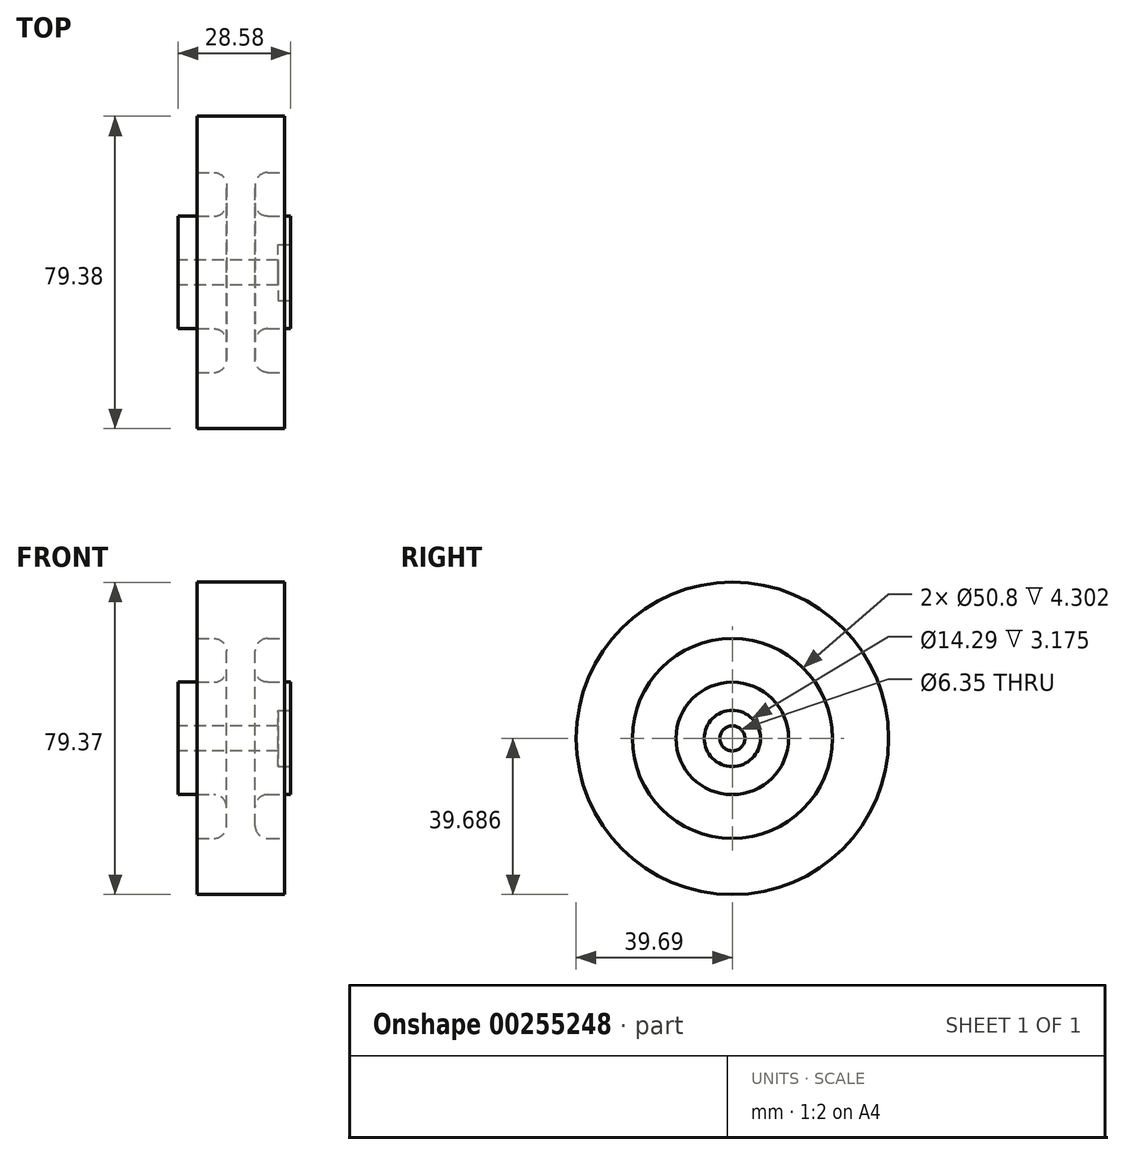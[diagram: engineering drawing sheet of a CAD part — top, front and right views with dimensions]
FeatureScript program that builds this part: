
annotation { "Feature Type Name" : "Feature", "Feature Type Description" : "" }
export const myFeature = defineFeature(function(context is Context, id is Id, definition is map)
    precondition{}
    {
        {
            var Q0;
            Q0=qCreatedBy(makeId("Front.planeOp"),FACE);
            var sketch = newSketch(context, id + "F0", { "sketchPlane" : qUnion([Q0])});
            skLineSegment(sketch, "E0", {"start": v(0, 0) * mm, "end": v(-12.7, 0) * mm});
            skLineSegment(sketch, "E1", {"start": v(-12.7, 0) * mm, "end": v(-12.7, 7.14) * mm});
            skLineSegment(sketch, "E2", {"start": v(-12.7, 7.14) * mm, "end": v(-6.81, 7.14) * mm});
            skLineSegment(sketch, "E3", {"start": v(-3.64, 10.32) * mm, "end": v(-3.64, 15.08) * mm});
            skLineSegment(sketch, "E4", {"start": v(-6.81, 18.26) * mm, "end": v(-11.11, 18.26) * mm});
            skLineSegment(sketch, "E5", {"start": v(-11.11, 18.26) * mm, "end": v(-11.11, 32.54) * mm});
            skLineSegment(sketch, "E6", {"start": v(-11.11, 32.54) * mm, "end": v(0, 32.54) * mm});
            skLineSegment(sketch, "E7", {"start": v(0, 32.54) * mm, "end": v(0, 0) * mm});
            skLineSegment(sketch, "E8", {"start": v(0, 0) * mm, "end": v(0, -7.14) * mm, "construction": true});
            skLineSegment(sketch, "E9", {"start": v(0, -7.14) * mm, "end": v(-25.49, -7.14) * mm, "construction": true});
            skPoint(sketch, "E10.visualSharp", {"position": v(-3.64, 18.26) * mm});
            skArc(sketch, "E10.filletArc", {"start": v(-3.64, 15.08) * mm, "mid": v(-4.56, 17.33) * mm, "end": v(-6.81, 18.26) * mm});
            skPoint(sketch, "E11.visualSharp", {"position": v(-3.64, 7.14) * mm});
            skArc(sketch, "E11.filletArc", {"start": v(-6.81, 7.14) * mm, "mid": v(-4.56, 8.07) * mm, "end": v(-3.64, 10.32) * mm});
            skLineSegment(sketch, "E12.MirrorCS", {"start": v(11.11, 32.54) * mm, "end": v(0, 32.54) * mm});
            skLineSegment(sketch, "E13.MirrorCS", {"start": v(11.11, 18.26) * mm, "end": v(11.11, 32.54) * mm});
            skLineSegment(sketch, "E14.MirrorCS", {"start": v(6.81, 18.26) * mm, "end": v(11.11, 18.26) * mm});
            skArc(sketch, "E15.MirrorCS", {"start": v(3.64, 15.08) * mm, "mid": v(4.56, 17.33) * mm, "end": v(6.81, 18.26) * mm});
            skLineSegment(sketch, "E16.MirrorCS", {"start": v(3.64, 10.32) * mm, "end": v(3.64, 15.08) * mm});
            skArc(sketch, "E17.MirrorCS", {"start": v(6.81, 7.14) * mm, "mid": v(4.56, 8.07) * mm, "end": v(3.64, 10.32) * mm});
            skLineSegment(sketch, "E18.MirrorCS", {"start": v(12.7, 7.14) * mm, "end": v(6.81, 7.14) * mm});
            skLineSegment(sketch, "E19.MirrorCS", {"start": v(12.7, 0) * mm, "end": v(12.7, 7.14) * mm});
            skLineSegment(sketch, "E20.MirrorCS", {"start": v(0, 0) * mm, "end": v(12.7, 0) * mm});
            skSolve(sketch);
        }
        {
            var Q0;
            Q0=makeQuery(id+"F0.imprint","IMPRINT",FACE,{"disambiguationData":[TD([[makeQuery(id+"F0.imprint","IMPRINT",EDGE,{"derivedFrom":sQuery(id+"F0.wireOp",EDGE,"E0")}),-1.0]])]});
            var Q1;
            Q1=makeQuery(id+"F0.imprint","IMPRINT",FACE,{"disambiguationData":[TD([[makeQuery(id+"F0.imprint","IMPRINT",EDGE,{"derivedFrom":sQuery(id+"F0.wireOp",EDGE,"E7")}),1.0]])]});
            var Q2;
            Q2=sQuery(id+"F0.wireOp",EDGE,"E9");
            revolve(context, id + "F1", {"entities" : qUnion([Q0, Q1]), "axis" : qUnion([Q2]), "revolveType" : RevolveType.FULL});
        }
        {
            var Q0;
            Q0=makeQuery(id+"F1.opRevolve","SWEPT_FACE",FACE,{"disambiguationData":[OSD([sQuery(id+"F0.wireOp",EDGE,"E1")])]});
            var sketch = newSketch(context, id + "F2", { "sketchPlane" : qUnion([Q0])});
            skCircle(sketch, "E21", {"center": v(0, -7.14) * mm, "radius": 3.18 * mm});
            skSolve(sketch);
        }
        {
            var Q0;
            Q0=makeQuery(id+"F2.imprint","IMPRINT",FACE,{"disambiguationData":[TD([[makeQuery(id+"F2.imprint","IMPRINT",EDGE,{"derivedFrom":sQuery(id+"F2.wireOp",EDGE,"E21")}),-1.0]])]});
            extrude(context, id + "F3", {"entities" : qUnion([Q0]), "oppositeDirection" : true, "depth" : 22.22 * mm});
        }
        {
            var Q0;
            Q0=makeQuery(id+"F1.opRevolve","SWEPT_FACE",FACE,{"disambiguationData":[OSD([sQuery(id+"F0.wireOp",EDGE,"E1")])]});
            var Q1;
            Q1=makeQuery(id+"F3.opExtrude","CAP_FACE",FACE,{"disambiguationData":[OSD([sQuery(id+"F0.wireOp",EDGE,"E0"),sQuery(id+"F0.wireOp",EDGE,"E1"),sQuery(id+"F2.wireOp",EDGE,"E21")])],"isStart":true});
            extrude(context, id + "F4", {"entities" : qUnion([Q0, Q1]), "operationType" : NewBodyOperationType.ADD, "depth" : 3.17 * mm});
        }
    });
